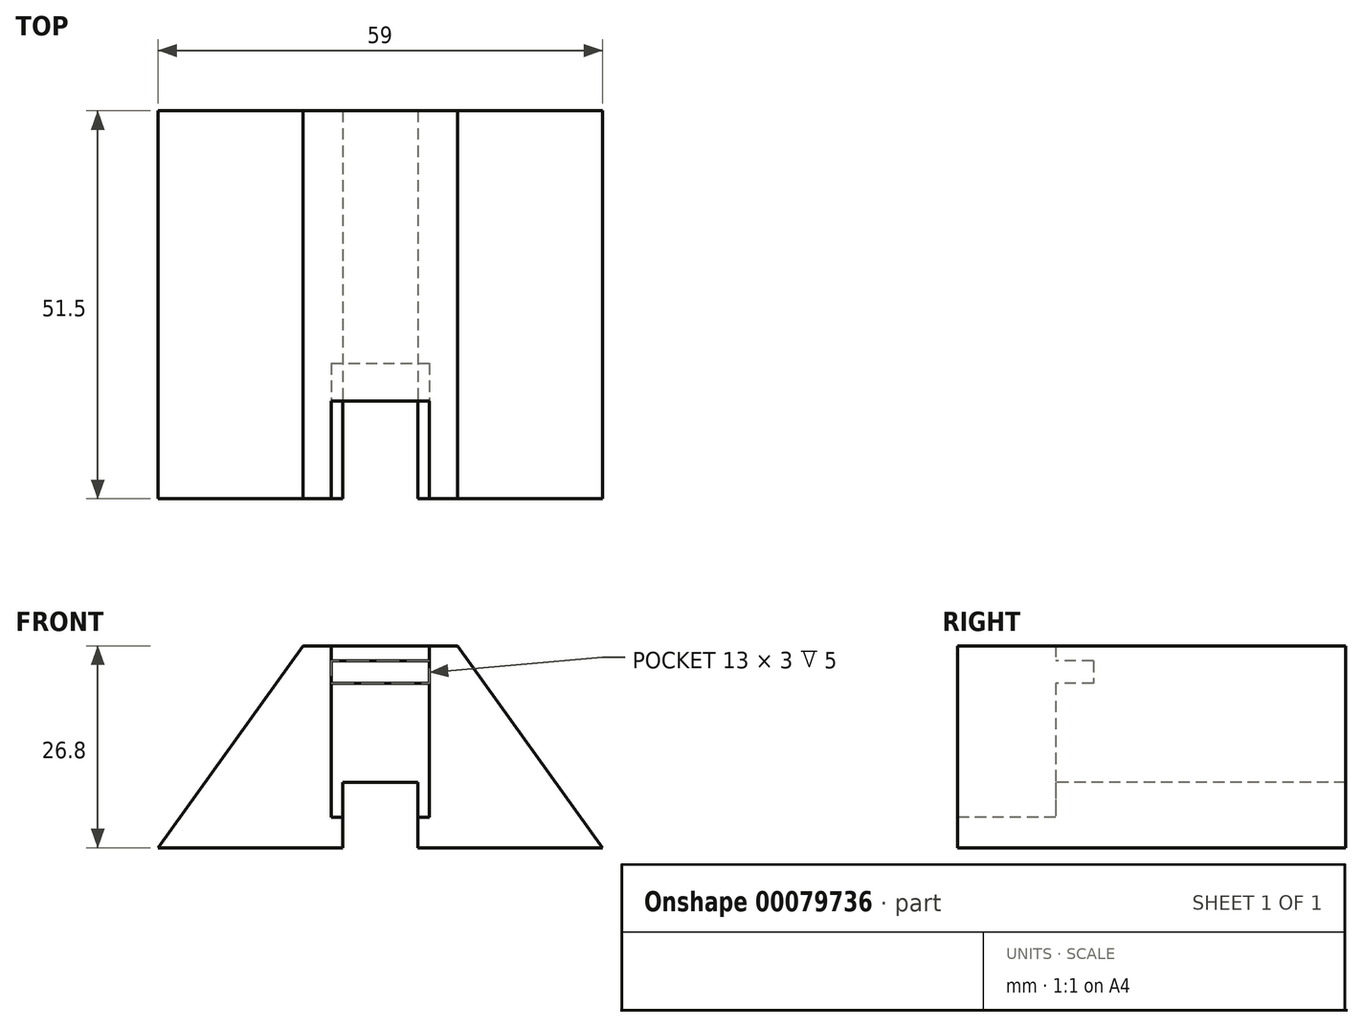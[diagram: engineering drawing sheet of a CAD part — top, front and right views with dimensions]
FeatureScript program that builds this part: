
annotation { "Feature Type Name" : "Feature", "Feature Type Description" : "" }
export const myFeature = defineFeature(function(context is Context, id is Id, definition is map)
    precondition{}
    {
        {
            var Q0;
            Q0=qCreatedBy(makeId("Top.planeOp"),FACE);
            var sketch = newSketch(context, id + "F0", { "sketchPlane" : qUnion([Q0])});
            skLineSegment(sketch, "E0.bottom", {"start": v(-29.5, 25.75) * mm, "end": v(29.5, 25.75) * mm});
            skLineSegment(sketch, "E0.top", {"start": v(-29.5, -25.75) * mm, "end": v(29.5, -25.75) * mm});
            skLineSegment(sketch, "E0.left", {"start": v(-29.5, 25.75) * mm, "end": v(-29.5, -25.75) * mm});
            skLineSegment(sketch, "E0.right", {"start": v(29.5, 25.75) * mm, "end": v(29.5, -25.75) * mm});
            skSolve(sketch);
        }
        {
            var Q0;
            Q0=makeQuery(id+"F0.imprint","IMPRINT",FACE,{"disambiguationData":[TD([[makeQuery(id+"F0.imprint","IMPRINT",EDGE,{"derivedFrom":sQuery(id+"F0.wireOp",EDGE,"E0.bottom")}),-1.0]])]});
            extrude(context, id + "F1", {"entities" : qUnion([Q0]), "depth" : 26.8 * mm});
        }
        {
            var Q0;
            Q0=makeQuery(id+"F1.opExtrude","SWEPT_FACE",FACE,{"disambiguationData":[OSD([sQuery(id+"F0.wireOp",EDGE,"E0.top")])]});
            var sketch = newSketch(context, id + "F2", { "sketchPlane" : qUnion([Q0])});
            skLineSegment(sketch, "E1", {"start": v(-29.5, 0) * mm, "end": v(-10.24, 26.8) * mm});
            skLineSegment(sketch, "E2", {"start": v(29.5, 0) * mm, "end": v(10.24, 26.8) * mm});
            skSolve(sketch);
        }
        {
            var Q0;
            {var subQ0=sQuery(id+"F2.wireOp",EDGE,"E1");Q0=makeQuery(id+"F2.imprint","IMPRINT",FACE,{"disambiguationData":[TD([[makeQuery(id+"F2.imprint","IMPRINT",EDGE,{"derivedFrom":subQ0}),1.0]])]});}
            var Q1;
            {var subQ0=sQuery(id+"F2.wireOp",EDGE,"E2");Q1=makeQuery(id+"F2.imprint","IMPRINT",FACE,{"disambiguationData":[TD([[makeQuery(id+"F2.imprint","IMPRINT",EDGE,{"derivedFrom":subQ0}),-1.0]])]});}
            extrude(context, id + "F3", {"entities" : qUnion([Q0, Q1]), "operationType" : NewBodyOperationType.REMOVE, "oppositeDirection" : true, "depth" : 55 * mm});
        }
        {
            var Q0;
            Q0=makeQuery(id+"F1.opExtrude","SWEPT_FACE",FACE,{"disambiguationData":[OSD([sQuery(id+"F0.wireOp",EDGE,"E0.top")])]});
            var sketch = newSketch(context, id + "F4", { "sketchPlane" : qUnion([Q0])});
            skLineSegment(sketch, "E3.bottom", {"start": v(-5, 8.67) * mm, "end": v(5, 8.67) * mm});
            skLineSegment(sketch, "E3.top", {"start": v(-5, 0) * mm, "end": v(5, 0) * mm});
            skLineSegment(sketch, "E3.left", {"start": v(-5, 8.67) * mm, "end": v(-5, 0) * mm});
            skLineSegment(sketch, "E3.right", {"start": v(5, 8.67) * mm, "end": v(5, 0) * mm});
            skSolve(sketch);
        }
        {
            var Q0;
            Q0 = qSketchRegion(id + "F4", true);
            extrude(context, id + "F5", {"entities" : qUnion([Q0]), "operationType" : NewBodyOperationType.REMOVE, "endBound" : BoundingType.THROUGH_ALL, "oppositeDirection" : true, "depth" : 25 * mm});
        }
        {
            var Q0;
            Q0=makeQuery(id+"F1.opExtrude","SWEPT_FACE",FACE,{"disambiguationData":[OSD([sQuery(id+"F0.wireOp",EDGE,"E0.top")])]});
            var sketch = newSketch(context, id + "F6", { "sketchPlane" : qUnion([Q0])});
            skLineSegment(sketch, "E4.bottom", {"start": v(-6.5, 26.8) * mm, "end": v(6.5, 26.8) * mm});
            skLineSegment(sketch, "E4.top", {"start": v(-6.5, 4.05) * mm, "end": v(6.5, 4.05) * mm});
            skLineSegment(sketch, "E4.left", {"start": v(-6.5, 26.8) * mm, "end": v(-6.5, 4.05) * mm});
            skLineSegment(sketch, "E4.right", {"start": v(6.5, 26.8) * mm, "end": v(6.5, 4.05) * mm});
            skSolve(sketch);
        }
        {
            var Q0;
            Q0=makeQuery(id+"F6.imprint","IMPRINT",FACE,{"disambiguationData":[TD([[makeQuery(id+"F6.imprint","IMPRINT",EDGE,{"derivedFrom":sQuery(id+"F6.wireOp",EDGE,"E4.bottom")}),-1.0]])]});
            extrude(context, id + "F7", {"entities" : qUnion([Q0]), "operationType" : NewBodyOperationType.REMOVE, "oppositeDirection" : true, "depth" : 13 * mm});
        }
        {
            var Q0;
            Q0=makeQuery(id+"F7.boolean.opBoolean","COPY",FACE,{"derivedFrom":makeQuery(id+"F7.opExtrude","CAP_FACE",FACE,{"disambiguationData":[OSD([sQuery(id+"F4.wireOp",EDGE,"E3.bottom"),sQuery(id+"F4.wireOp",EDGE,"E3.left"),sQuery(id+"F4.wireOp",EDGE,"E3.right"),sQuery(id+"F6.wireOp",EDGE,"E4.bottom"),sQuery(id+"F6.wireOp",EDGE,"E4.top"),sQuery(id+"F6.wireOp",EDGE,"E4.left"),sQuery(id+"F6.wireOp",EDGE,"E4.right")])],"isStart":false})});
            var sketch = newSketch(context, id + "F8", { "sketchPlane" : qUnion([Q0])});
            skLineSegment(sketch, "E5.bottom", {"start": v(-6.5, 24.8) * mm, "end": v(6.5, 24.8) * mm});
            skLineSegment(sketch, "E5.top", {"start": v(-6.5, 21.8) * mm, "end": v(6.5, 21.8) * mm});
            skLineSegment(sketch, "E5.left", {"start": v(-6.5, 24.8) * mm, "end": v(-6.5, 21.8) * mm});
            skLineSegment(sketch, "E5.right", {"start": v(6.5, 24.8) * mm, "end": v(6.5, 21.8) * mm});
            skSolve(sketch);
        }
        {
            var Q0;
            Q0 = qSketchRegion(id + "F8", true);
            extrude(context, id + "F9", {"entities" : qUnion([Q0]), "operationType" : NewBodyOperationType.REMOVE, "oppositeDirection" : true, "depth" : 5 * mm});
        }
    });
